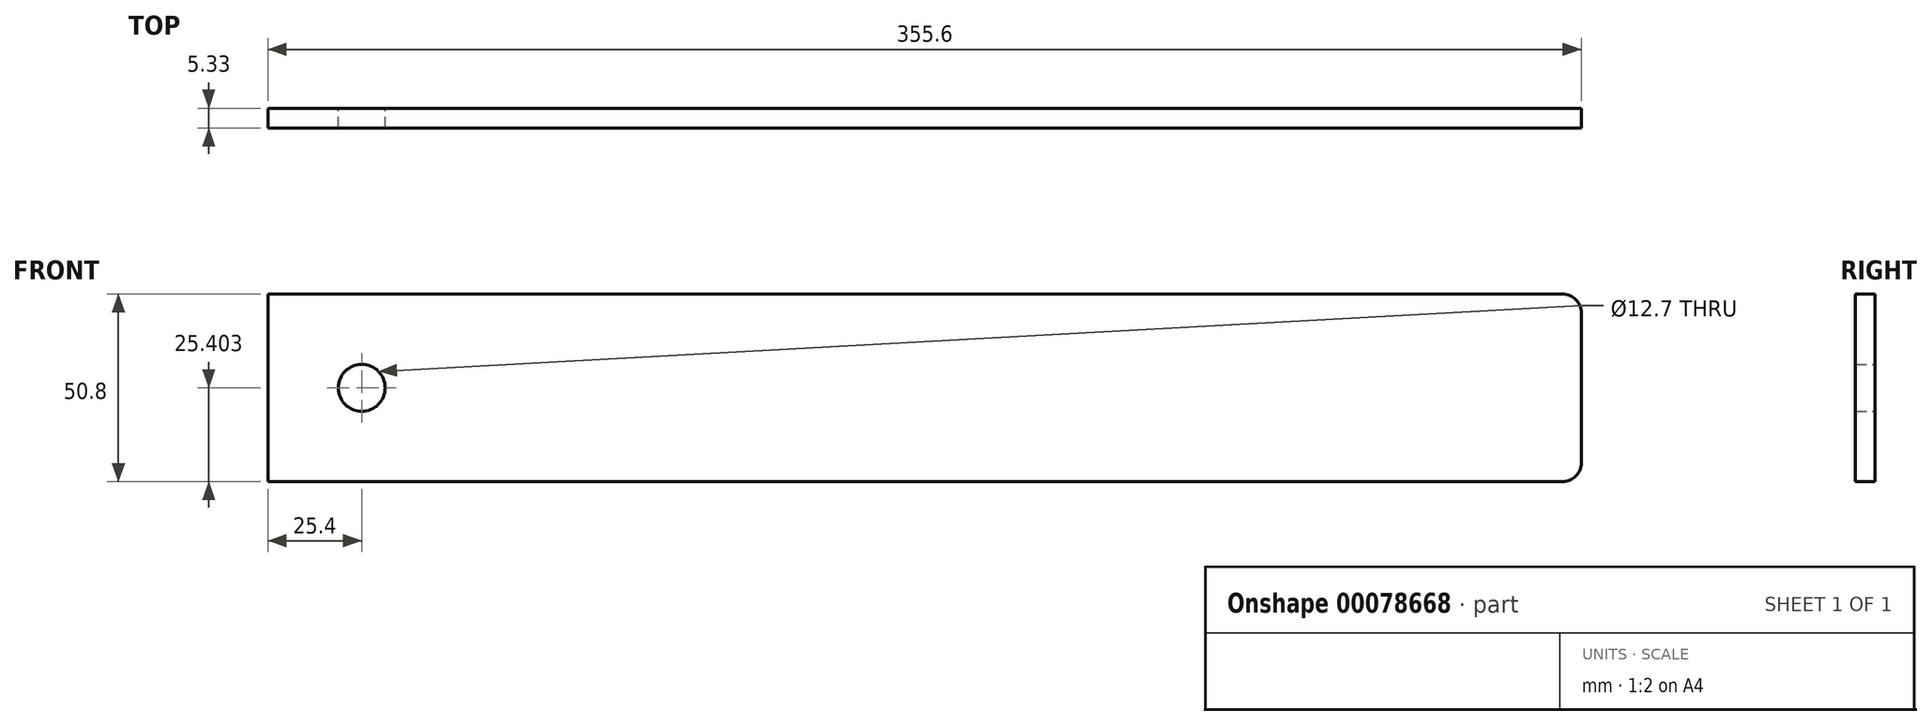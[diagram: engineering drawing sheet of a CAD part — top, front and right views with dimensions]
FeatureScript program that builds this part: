
annotation { "Feature Type Name" : "Feature", "Feature Type Description" : "" }
export const myFeature = defineFeature(function(context is Context, id is Id, definition is map)
    precondition{}
    {
        {
            var Q0;
            Q0=qCreatedBy(makeId("Front.planeOp"),FACE);
            var sketch = newSketch(context, id + "F0", { "sketchPlane" : qUnion([Q0])});
            skLineSegment(sketch, "E0.bottom", {"start": v(-153.28, 69.94) * mm, "end": v(202.32, 69.94) * mm});
            skLineSegment(sketch, "E0.top", {"start": v(-153.28, 19.14) * mm, "end": v(202.32, 19.14) * mm});
            skLineSegment(sketch, "E0.left", {"start": v(-153.28, 69.94) * mm, "end": v(-153.28, 19.14) * mm});
            skLineSegment(sketch, "E0.right", {"start": v(202.32, 69.94) * mm, "end": v(202.32, 19.14) * mm});
            skCircle(sketch, "E1", {"center": v(-127.88, 44.54) * mm, "radius": 6.35 * mm});
            skPoint(sketch, "E1.centerSnap0", {"position": v(-153.28, 44.54) * mm});
            skSolve(sketch);
        }
        {
            var Q0;
            Q0=makeQuery(id+"F0.imprint","IMPRINT",FACE,{"disambiguationData":[TD([[makeQuery(id+"F0.imprint","IMPRINT",EDGE,{"derivedFrom":sQuery(id+"F0.wireOp",EDGE,"E0.bottom")}),-1.0]])]});
            extrude(context, id + "F1", {"entities" : qUnion([Q0]), "depth" : 5.33 * mm});
        }
        {
            var Q0;
            Q0=makeQuery(id+"F1.opExtrude","SWEPT_EDGE",EDGE,{"disambiguationData":[OSD([sQuery(id+"F0.wireOp",EDGE,"E0.bottom"),sQuery(id+"F0.wireOp",EDGE,"E0.right")])]});
            var Q1;
            Q1=makeQuery(id+"F1.opExtrude","SWEPT_EDGE",EDGE,{"disambiguationData":[OSD([sQuery(id+"F0.wireOp",EDGE,"E0.top"),sQuery(id+"F0.wireOp",EDGE,"E0.right")])]});
            fillet(context, id + "F2", {"entities" : qUnion([Q0, Q1]), "radius" : 5.08 * mm, "tangentPropagation" : true, "allowEdgeOverflow" : false});
        }
    });
